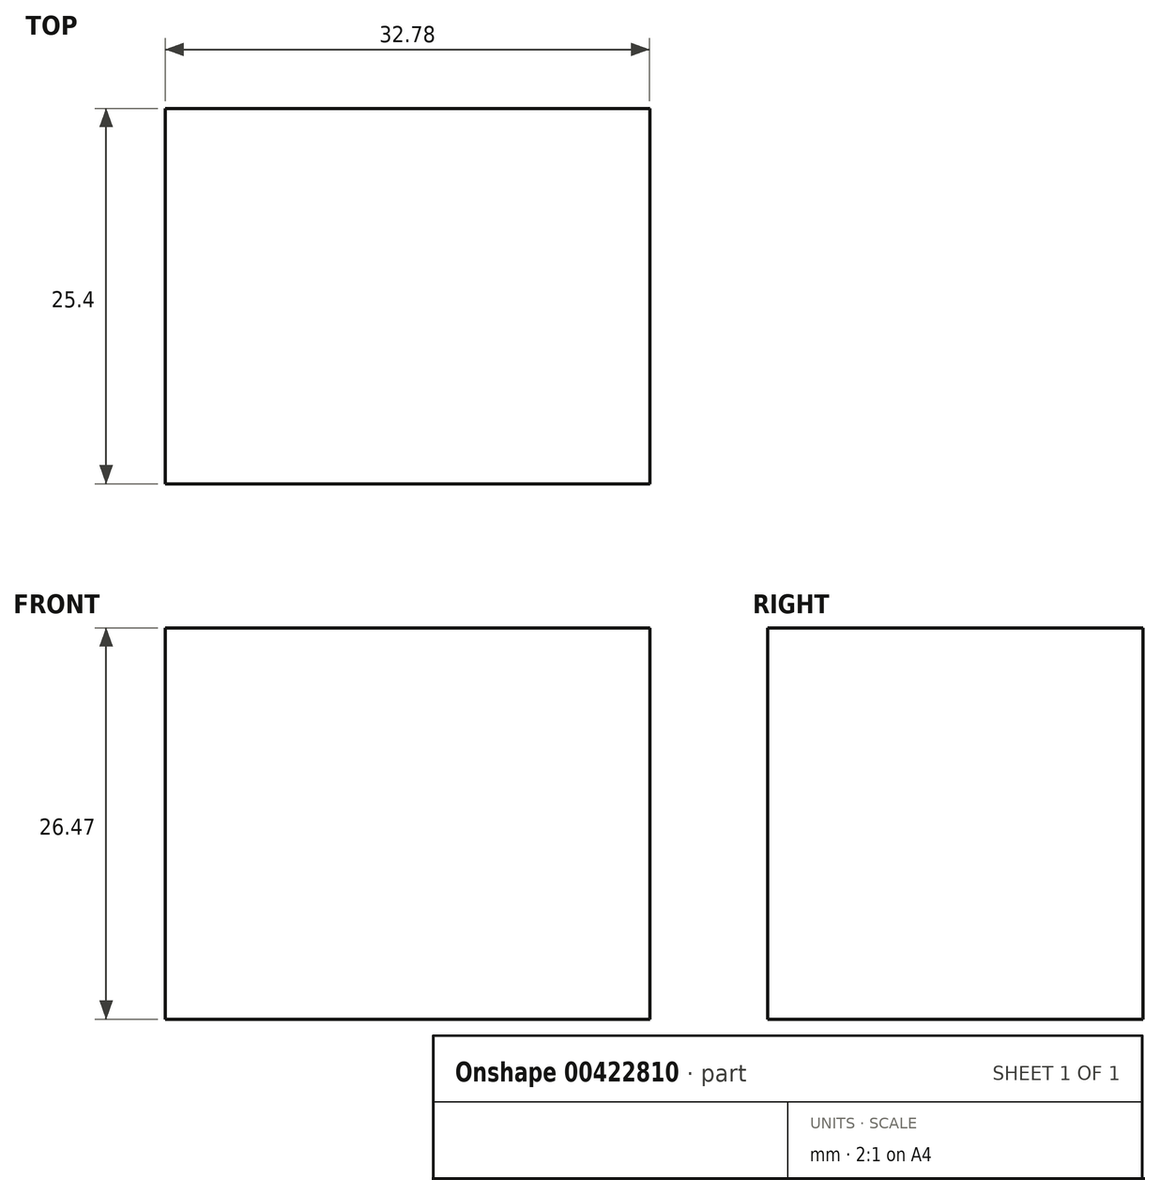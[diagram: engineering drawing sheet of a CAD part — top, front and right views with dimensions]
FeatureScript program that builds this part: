
annotation { "Feature Type Name" : "Feature", "Feature Type Description" : "" }
export const myFeature = defineFeature(function(context is Context, id is Id, definition is map)
    precondition{}
    {
        {
            var Q0;
            Q0=qCreatedBy(makeId("Front.planeOp"),FACE);
            var sketch = newSketch(context, id + "F0", { "sketchPlane" : qUnion([Q0])});
            skLineSegment(sketch, "E0.bottom", {"start": v(-42.41, 11.13) * mm, "end": v(-9.63, 11.13) * mm});
            skLineSegment(sketch, "E0.top", {"start": v(-42.41, 37.6) * mm, "end": v(-9.63, 37.6) * mm});
            skLineSegment(sketch, "E0.left", {"start": v(-42.41, 11.13) * mm, "end": v(-42.41, 37.6) * mm});
            skLineSegment(sketch, "E0.right", {"start": v(-9.63, 11.13) * mm, "end": v(-9.63, 37.6) * mm});
            skSolve(sketch);
        }
        {
            var Q0;
            Q0=makeQuery(id+"F0.imprint","IMPRINT",FACE,{"disambiguationData":[TD([[makeQuery(id+"F0.imprint","IMPRINT",EDGE,{"derivedFrom":sQuery(id+"F0.wireOp",EDGE,"E0.bottom")}),1.0]])]});
            extrude(context, id + "F1", {"entities" : qUnion([Q0]), "depth" : 25.4 * mm});
        }
    });
